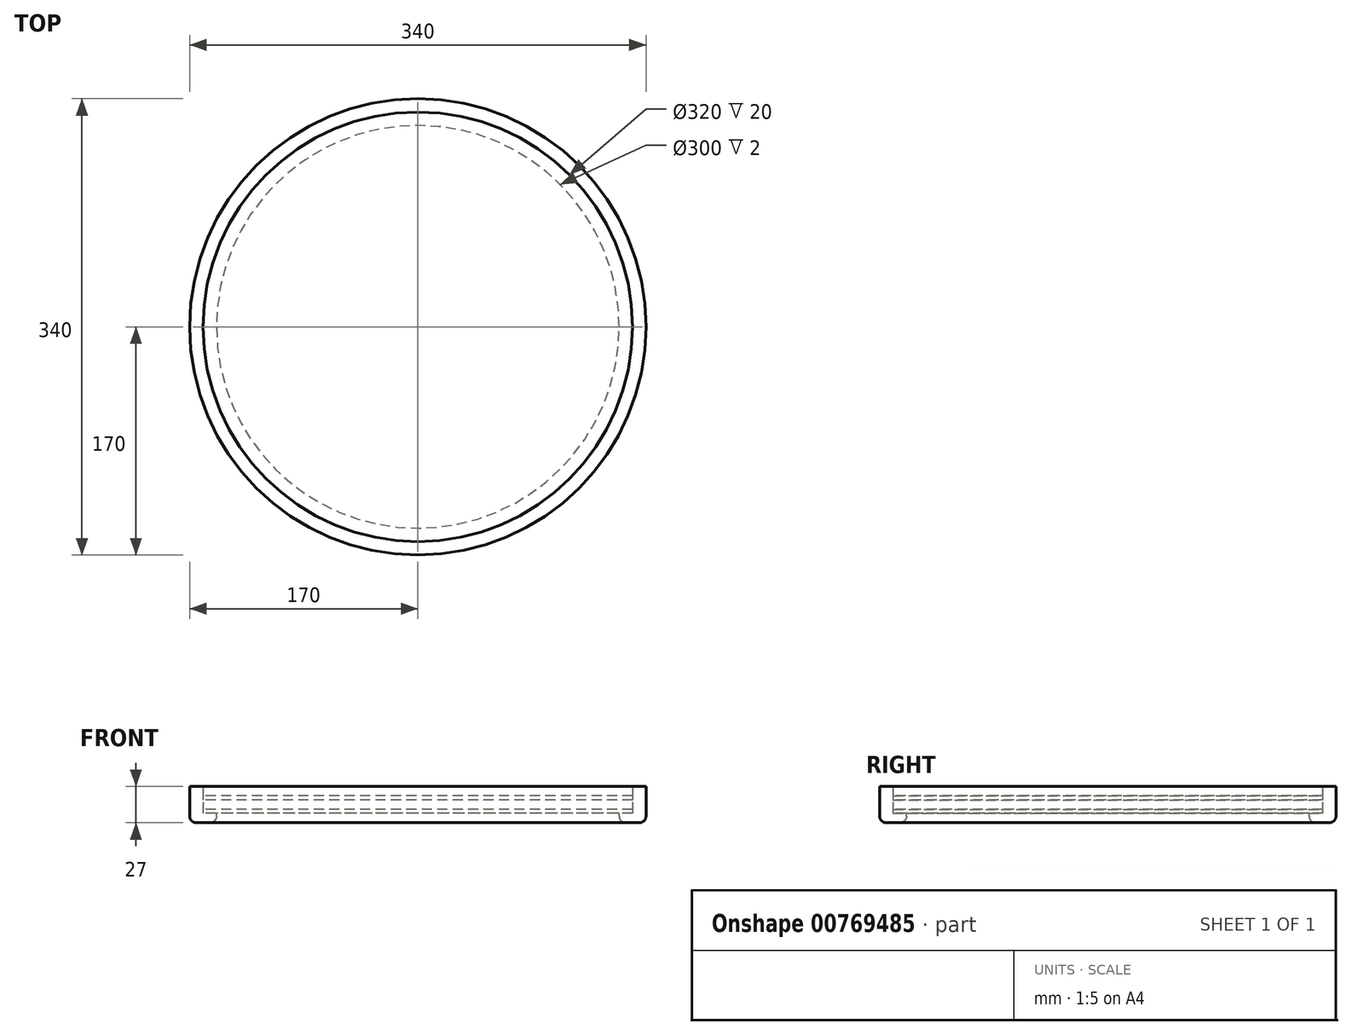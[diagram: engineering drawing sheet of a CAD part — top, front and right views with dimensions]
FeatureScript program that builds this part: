
annotation { "Feature Type Name" : "Feature", "Feature Type Description" : "" }
export const myFeature = defineFeature(function(context is Context, id is Id, definition is map)
    precondition{}
    {
        {
            var Q0;
            Q0=qCreatedBy(makeId("Top.planeOp"),FACE);
            var sketch = newSketch(context, id + "F0", { "sketchPlane" : qUnion([Q0])});
            skCircle(sketch, "E0", {"center": v(0, 0) * mm, "radius": 160 * mm});
            skCircle(sketch, "E1.0", {"center": v(0, 0) * mm, "radius": 170 * mm});
            skCircle(sketch, "E2.0", {"center": v(0, 0) * mm, "radius": 150 * mm});
            skSolve(sketch);
        }
        {
            var Q0;
            Q0=makeQuery(id+"F0.imprint","IMPRINT",FACE,{"disambiguationData":[TD([[makeQuery(id+"F0.imprint","IMPRINT",EDGE,{"derivedFrom":sQuery(id+"F0.wireOp",EDGE,"E0")}),-1.0]])]});
            extrude(context, id + "F1", {"entities" : qUnion([Q0]), "depth" : 20 * mm, "offsetDistance" : 25 * mm, "hasSecondDirection" : true, "secondDirectionOppositeDirection" : true, "secondDirectionDepth" : 7 * mm});
        }
        {
            var Q0;
            Q0=makeQuery(id+"F0.imprint","IMPRINT",FACE,{"disambiguationData":[TD([[makeQuery(id+"F0.imprint","IMPRINT",EDGE,{"derivedFrom":sQuery(id+"F0.wireOp",EDGE,"E0")}),1.0]])]});
            extrude(context, id + "F2", {"entities" : qUnion([Q0]), "operationType" : NewBodyOperationType.ADD, "oppositeDirection" : true, "depth" : 7 * mm, "offsetDistance" : 25 * mm});
        }
        {
            var Q0;
            Q0=makeQuery(id+"F1.opExtrude","CAP_EDGE",EDGE,{"disambiguationData":[OSD([sQuery(id+"F0.wireOp",EDGE,"E1.0")])],"isStart":true});
            fillet(context, id + "F3", {"entities" : qUnion([Q0]), "radius" : 5 * mm, "tangentPropagation" : true, "allowEdgeOverflow" : false});
        }
        {
            var Q0;
            Q0=makeQuery(id+"F0.imprint","IMPRINT",FACE,{"disambiguationData":[TD([[makeQuery(id+"F0.imprint","IMPRINT",EDGE,{"derivedFrom":sQuery(id+"F0.wireOp",EDGE,"E0")}),1.0]])]});
            var Q1;
            Q1=makeQuery(id+"F0.imprint","IMPRINT",FACE,{"disambiguationData":[TD([[makeQuery(id+"F0.imprint","IMPRINT",EDGE,{"derivedFrom":sQuery(id+"F0.wireOp",EDGE,"E2.0")}),1.0]])]});
            extrude(context, id + "F4", {"entities" : qUnion([Q0, Q1]), "depth" : 3 * mm, "offsetDistance" : 25 * mm});
        }
        {
            var Q0;
            Q0=makeQuery(id+"F4.opExtrude","SWEPT_BODY",BODY,{"disambiguationData":[OSD([sQuery(id+"F0.wireOp",EDGE,"E0")])]});
            transform(context, id + "F5", {"entities" : qUnion([Q0]), "transformType" : TransformType.TRANSLATION_3D, "dx" : 0 * mm, "dy" : 0 * mm, "dz" : 10 * mm, "makeCopy" : true});
        }
        {
            var Q0;
            Q0=makeQuery(id+"F2.opExtrude","CAP_EDGE",EDGE,{"disambiguationData":[OSD([sQuery(id+"F0.wireOp",EDGE,"E2.0")])],"isStart":false});
            fillet(context, id + "F6", {"entities" : qUnion([Q0]), "radius" : 5 * mm, "tangentPropagation" : true, "allowEdgeOverflow" : false});
        }
    });
